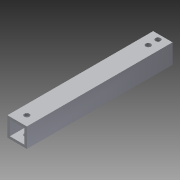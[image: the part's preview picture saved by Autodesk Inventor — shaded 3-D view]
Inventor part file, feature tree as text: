
AUTODESK INVENTOR PART (.ipt)
format: ipt  version: 2013 (Build 170138000, 138)  size: 102,912 bytes
history: native  units: in
note: dims shown in document units (in); Inventor stores cm internally (conversion verified against a paired STEP export)
features: reference x4, extrude x3, sketch x3
ambient origin geometry x8: Origin, YZ Plane, XZ Plane, XY Plane, X Axis, Y Axis, Z Axis, Center Point
bodies: Solid1 (feature_tree)
feature tree (10):
  extrude  "Extrusion1"  Depth=1.0in
  extrude  "Extrusion2"  Depth=7.5in TaperAngle=0.0deg
  extrude  "Extrusion3"  Depth=1.0in TaperAngle=0.0deg
  sketch  "Sketch1"  dims[d0=1.0in d2=1.0in]
  sketch  "Sketch2"  dims[d3=0.125in d4=7.5in d5=0.0in]
  reference  "Reference1"
  reference  "Reference2"
  sketch  "Sketch3"  dims[d6=1.0in d7=0.0in d8=1.0in d9=0.0in]
  reference  "Reference3"
  reference  "Reference4"
